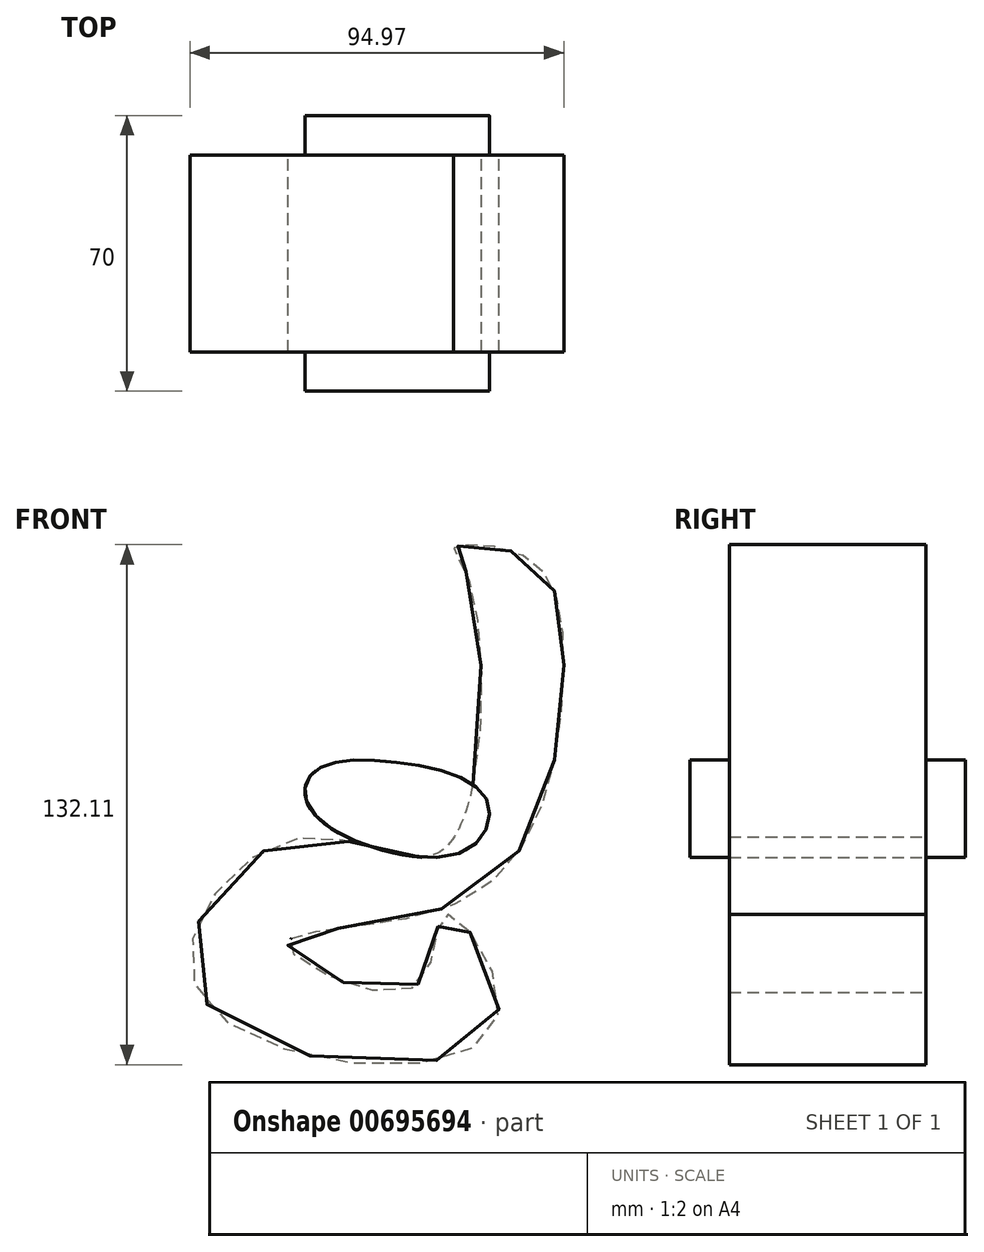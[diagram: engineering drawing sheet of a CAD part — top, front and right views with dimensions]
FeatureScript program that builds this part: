
annotation { "Feature Type Name" : "Feature", "Feature Type Description" : "" }
export const myFeature = defineFeature(function(context is Context, id is Id, definition is map)
    precondition{}
    {
        {
            var Q0;
            Q0=qCreatedBy(makeId("Front.planeOp"),FACE);
            var sketch = newSketch(context, id + "F0", { "sketchPlane" : qUnion([Q0])});
            skFitSpline(sketch, "E0", {"points": [v(38.97, 50.03) * mm, v(33.08, -19.48) * mm, v(-4.67, -16.98) * mm, v(-28.82, -56.94) * mm, v(45.7, -65.04) * mm, v(33.54, -36.2) * mm, v(25.46, -54.6) * mm, v(-6.6, -44.02) * mm, v(38.72, -32.17) * mm, v(63.38, 23.51) * mm, v(54.4, 54.29) * mm, v(35.77, 57.06) * mm, v(38.97, 50.03) * mm]});
            skSolve(sketch);
        }
        {
            var Q0;
            Q0=makeQuery(id+"F0.imprint","IMPRINT",FACE,{"disambiguationData":[TD([[makeQuery(id+"F0.imprint","IMPRINT",EDGE,{"derivedFrom":sQuery(id+"F0.wireOp",EDGE,"E0")}),1.0]])]});
            extrude(context, id + "F1", {"entities" : qUnion([Q0]), "depth" : 50 * mm, "offsetDistance" : 25 * mm});
        }
        {
            var Q0;
            Q0=qCreatedBy(makeId("Front.planeOp"),FACE);
            var sketch = newSketch(context, id + "F2", { "sketchPlane" : qUnion([Q0])});
            skFitSpline(sketch, "E1", {"points": [v(43.78, -6.88) * mm, v(21.18, 2.46) * mm, v(0, 0) * mm, v(0, -10.62) * mm, v(37.51, -20.45) * mm, v(43.78, -6.88) * mm]});
            skSolve(sketch);
        }
        {
            var Q0;
            Q0=makeQuery(id+"F2.imprint","IMPRINT",FACE,{"disambiguationData":[TD([[makeQuery(id+"F2.imprint","IMPRINT",EDGE,{"derivedFrom":sQuery(id+"F2.wireOp",EDGE,"E1")}),1.0]])]});
            extrude(context, id + "F3", {"entities" : qUnion([Q0]), "operationType" : NewBodyOperationType.ADD, "oppositeDirection" : true, "depth" : 10 * mm, "offsetDistance" : 25 * mm});
        }
        {
            var Q0;
            Q0=qCreatedBy(makeId("Front.planeOp"),FACE);
            cPlane(context, id + "F4", {"entities" : qUnion([Q0]), "cplaneType" : CPlaneType.OFFSET, "offset" : 25 * mm, "width" : 150 * mm, "height" : 150 * mm});
        }
        {
            var Q0;
            Q0=makeQuery(id+"F1.opExtrude","SWEPT_BODY",BODY,{"disambiguationData":[OSD([sQuery(id+"F0.wireOp",EDGE,"E0")])]});
            var Q1;
            Q1=qCreatedBy(id+"F4.planeOp",FACE);
            mirror(context, id + "F5", {"operationType" : NewBodyOperationType.ADD, "entities" : qUnion([Q0]), "mirrorPlane" : qUnion([Q1])});
        }
    });
